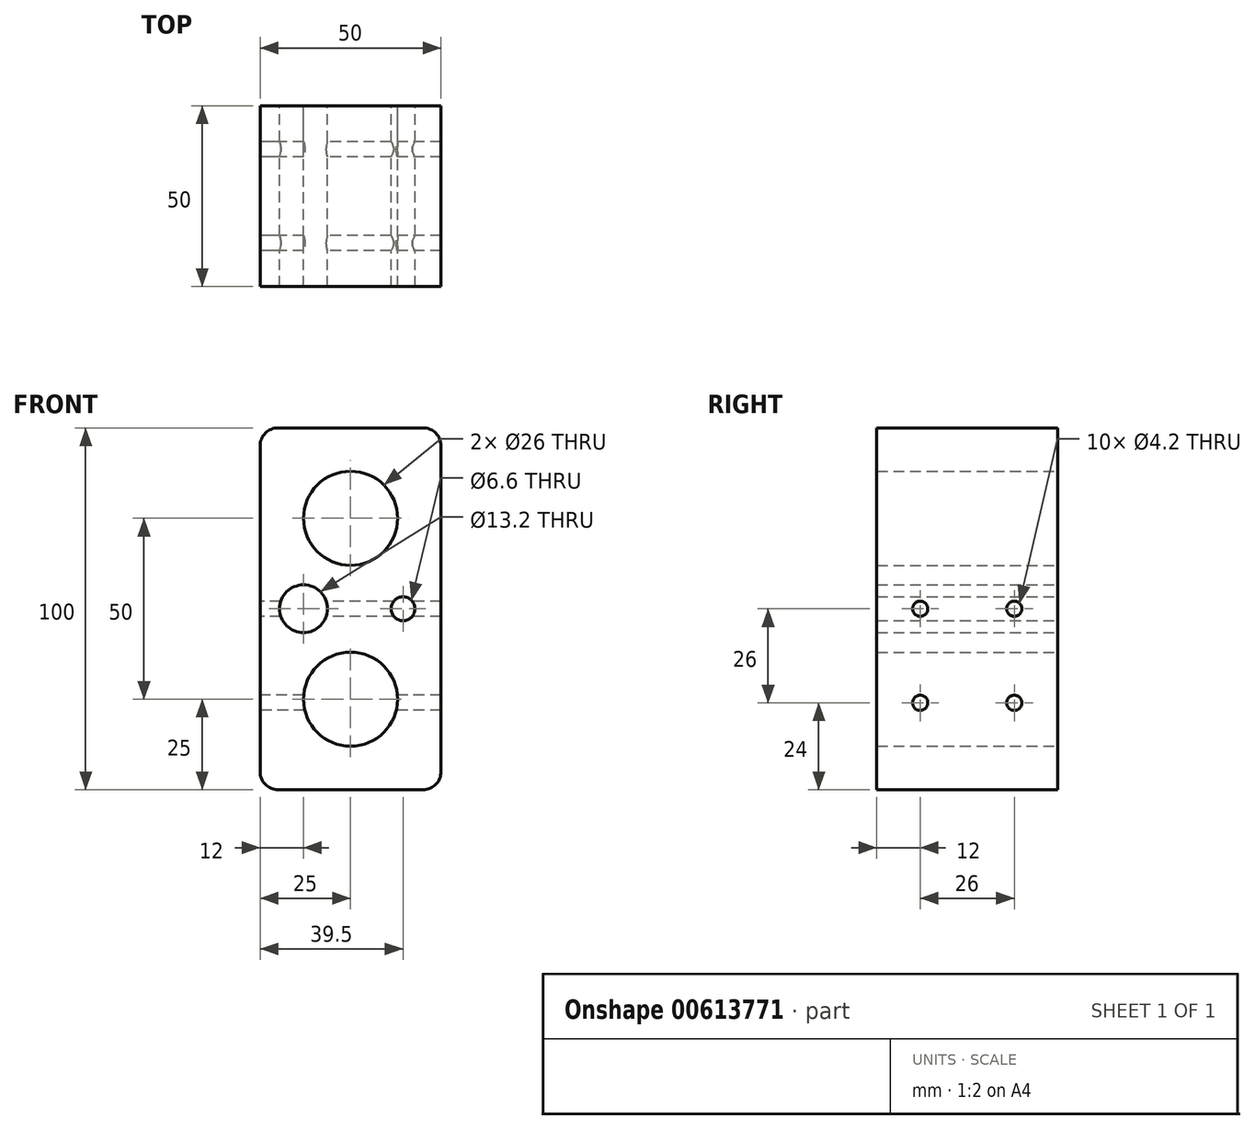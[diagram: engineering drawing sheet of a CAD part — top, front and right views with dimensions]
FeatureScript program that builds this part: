
annotation { "Feature Type Name" : "Feature", "Feature Type Description" : "" }
export const myFeature = defineFeature(function(context is Context, id is Id, definition is map)
    precondition{}
    {
        {
            var Q0;
            Q0=qCreatedBy(makeId("Front.planeOp"),FACE);
            var sketch = newSketch(context, id + "F0", { "sketchPlane" : qUnion([Q0])});
            skLineSegment(sketch, "E0.bottom", {"start": v(-25, 50) * mm, "end": v(25, 50) * mm});
            skLineSegment(sketch, "E0.top", {"start": v(-25, -50) * mm, "end": v(25, -50) * mm});
            skLineSegment(sketch, "E0.left", {"start": v(-25, 50) * mm, "end": v(-25, -50) * mm});
            skLineSegment(sketch, "E0.right", {"start": v(25, 50) * mm, "end": v(25, -50) * mm});
            skPoint(sketch, "E1", {"position": v(14.5, 0) * mm});
            skPoint(sketch, "E2", {"position": v(-13, 0) * mm});
            skPoint(sketch, "E3", {"position": v(0, 25) * mm});
            skPoint(sketch, "E4", {"position": v(0, -25) * mm});
            skSolve(sketch);
        }
        {
            var Q0;
            Q0 = qSketchRegion(id + "F0", true);
            extrude(context, id + "F1", {"entities" : qUnion([Q0]), "depth" : 50 * mm, "offsetDistance" : 25 * mm});
        }
        {
            var Q0;
            Q0=sQuery(id+"F0.wireOp",VERTEX,"E3");
            var Q1;
            Q1=sQuery(id+"F0.wireOp",VERTEX,"E4");
            var Q2;
            Q2=makeQuery(id+"F1.opExtrude","SWEPT_BODY",BODY,{"disambiguationData":[OSD([sQuery(id+"F0.wireOp",EDGE,"E0.bottom"),sQuery(id+"F0.wireOp",EDGE,"E0.top"),sQuery(id+"F0.wireOp",EDGE,"E0.left"),sQuery(id+"F0.wireOp",EDGE,"E0.right")])]});
            hole(context, id + "F2", {"style" : HoleStyle.SIMPLE, "endStyle" : HoleEndStyle.THROUGH, "oppositeDirection" : true, "standardTappedOrClearance" : lookupTablePath({ "standard" : "ISO", "size" : "26", "type" : "Drilled" }), "standardBlindInLast" : lookupTablePath({ "standard" : "ISO", "size" : "26", "type" : "Drilled" }), "holeDiameter" : 26 * mm, "majorDiameter" : 5 * mm, "isTappedThrough" : true, "tappedDepth" : 12 * mm, "tapClearance" : 3, "locations" : qUnion([Q0, Q1]), "scope" : qUnion([Q2])});
        }
        {
            var Q0;
            Q0=sQuery(id+"F0.wireOp",VERTEX,"E1");
            var Q1;
            Q1=makeQuery(id+"F1.opExtrude","SWEPT_BODY",BODY,{"disambiguationData":[OSD([sQuery(id+"F0.wireOp",EDGE,"E0.bottom"),sQuery(id+"F0.wireOp",EDGE,"E0.top"),sQuery(id+"F0.wireOp",EDGE,"E0.left"),sQuery(id+"F0.wireOp",EDGE,"E0.right")])]});
            hole(context, id + "F3", {"style" : HoleStyle.SIMPLE, "endStyle" : HoleEndStyle.THROUGH, "oppositeDirection" : true, "standardTappedOrClearance" : lookupTablePath({ "standard" : "ISO", "fit" : "Normal", "size" : "M6", "type" : "Clearance" }), "standardBlindInLast" : lookupTablePath({ "fit" : "Standard", "standard" : "ISO", "size" : "M6", "type" : "Clearance" }), "holeDiameter" : 6.6 * mm, "majorDiameter" : 5 * mm, "isTappedThrough" : true, "tappedDepth" : 12 * mm, "tapClearance" : 3, "locations" : qUnion([Q0]), "scope" : qUnion([Q1])});
        }
        {
            var Q0;
            Q0=sQuery(id+"F0.wireOp",VERTEX,"E2");
            var Q1;
            Q1=makeQuery(id+"F1.opExtrude","SWEPT_BODY",BODY,{"disambiguationData":[OSD([sQuery(id+"F0.wireOp",EDGE,"E0.bottom"),sQuery(id+"F0.wireOp",EDGE,"E0.top"),sQuery(id+"F0.wireOp",EDGE,"E0.left"),sQuery(id+"F0.wireOp",EDGE,"E0.right")])]});
            hole(context, id + "F4", {"style" : HoleStyle.SIMPLE, "endStyle" : HoleEndStyle.THROUGH, "oppositeDirection" : true, "standardTappedOrClearance" : lookupTablePath({ "standard" : "ISO", "engagement" : "50%", "pitch" : "1.25 mm", "size" : "M14", "type" : "Tapped" }), "standardBlindInLast" : lookupTablePath({ "standard" : "ISO", "engagement" : "50%", "pitch" : "1.25 mm", "size" : "M14", "type" : "Tapped" }), "holeDiameter" : 13.2 * mm, "majorDiameter" : 14 * mm, "showTappedDepth" : true, "isTappedThrough" : true, "tappedDepth" : 12 * mm, "tapClearance" : 3, "locations" : qUnion([Q0]), "scope" : qUnion([Q1])});
        }
        {
            var Q0;
            Q0=makeQuery(id+"F1.opExtrude","SWEPT_EDGE",EDGE,{"disambiguationData":[OSD([sQuery(id+"F0.wireOp",EDGE,"E0.bottom"),sQuery(id+"F0.wireOp",EDGE,"E0.left")])]});
            var Q1;
            Q1=makeQuery(id+"F1.opExtrude","SWEPT_EDGE",EDGE,{"disambiguationData":[OSD([sQuery(id+"F0.wireOp",EDGE,"E0.bottom"),sQuery(id+"F0.wireOp",EDGE,"E0.right")])]});
            var Q2;
            Q2=makeQuery(id+"F1.opExtrude","SWEPT_EDGE",EDGE,{"disambiguationData":[OSD([sQuery(id+"F0.wireOp",EDGE,"E0.top"),sQuery(id+"F0.wireOp",EDGE,"E0.right")])]});
            var Q3;
            Q3=makeQuery(id+"F1.opExtrude","SWEPT_EDGE",EDGE,{"disambiguationData":[OSD([sQuery(id+"F0.wireOp",EDGE,"E0.top"),sQuery(id+"F0.wireOp",EDGE,"E0.left")])]});
            fillet(context, id + "F5", {"entities" : qUnion([Q0, Q1, Q2, Q3]), "radius" : 5 * mm, "tangentPropagation" : true, "allowEdgeOverflow" : false});
        }
        {
            var Q0;
            Q0=makeQuery(id+"F1.opExtrude","SWEPT_FACE",FACE,{"disambiguationData":[OSD([sQuery(id+"F0.wireOp",EDGE,"E0.left")])]});
            var sketch = newSketch(context, id + "F6", { "sketchPlane" : qUnion([Q0])});
            skPoint(sketch, "E5", {"position": v(12, 0) * mm});
            skPoint(sketch, "E6", {"position": v(38, 0) * mm});
            skPoint(sketch, "E7", {"position": v(12, -26) * mm});
            skPoint(sketch, "E8", {"position": v(38, -26) * mm});
            skSolve(sketch);
        }
        {
            var Q0;
            Q0=sQuery(id+"F6.wireOp",VERTEX,"E5");
            var Q1;
            Q1=sQuery(id+"F6.wireOp",VERTEX,"E6");
            var Q2;
            Q2=makeQuery(id+"F1.opExtrude","SWEPT_BODY",BODY,{"disambiguationData":[OSD([sQuery(id+"F0.wireOp",EDGE,"E0.bottom"),sQuery(id+"F0.wireOp",EDGE,"E0.top"),sQuery(id+"F0.wireOp",EDGE,"E0.left"),sQuery(id+"F0.wireOp",EDGE,"E0.right")])]});
            hole(context, id + "F7", {"style" : HoleStyle.SIMPLE, "endStyle" : HoleEndStyle.BLIND, "standardTappedOrClearance" : lookupTablePath({ "standard" : "ISO", "engagement" : "75%", "pitch" : "0.8 mm", "size" : "M5", "type" : "Tapped" }), "standardBlindInLast" : lookupTablePath({ "standard" : "ISO", "engagement" : "75%", "pitch" : "0.8 mm", "size" : "M5", "type" : "Tapped" }), "holeDiameter" : 4.2 * mm, "majorDiameter" : 5 * mm, "showTappedDepth" : true, "holeDepth" : 52.4 * mm, "isTappedThrough" : true, "tappedDepth" : 50 * mm, "tapClearance" : 3, "locations" : qUnion([Q0, Q1]), "scope" : qUnion([Q2])});
        }
        {
            var Q0;
            Q0=sQuery(id+"F6.wireOp",VERTEX,"E7");
            var Q1;
            Q1=sQuery(id+"F6.wireOp",VERTEX,"E8");
            var Q2;
            Q2=makeQuery(id+"F1.opExtrude","SWEPT_BODY",BODY,{"disambiguationData":[OSD([sQuery(id+"F0.wireOp",EDGE,"E0.bottom"),sQuery(id+"F0.wireOp",EDGE,"E0.top"),sQuery(id+"F0.wireOp",EDGE,"E0.left"),sQuery(id+"F0.wireOp",EDGE,"E0.right")])]});
            hole(context, id + "F8", {"style" : HoleStyle.SIMPLE, "endStyle" : HoleEndStyle.BLIND, "standardTappedOrClearance" : lookupTablePath({ "standard" : "ISO", "engagement" : "75%", "pitch" : "0.8 mm", "size" : "M5", "type" : "Tapped" }), "standardBlindInLast" : lookupTablePath({ "standard" : "ISO", "engagement" : "75%", "pitch" : "0.8 mm", "size" : "M5", "type" : "Tapped" }), "holeDiameter" : 4.2 * mm, "majorDiameter" : 5 * mm, "showTappedDepth" : true, "holeDepth" : 50 * mm, "isTappedThrough" : true, "tappedDepth" : 47.6 * mm, "tapClearance" : 3, "locations" : qUnion([Q0, Q1]), "scope" : qUnion([Q2])});
        }
    });
